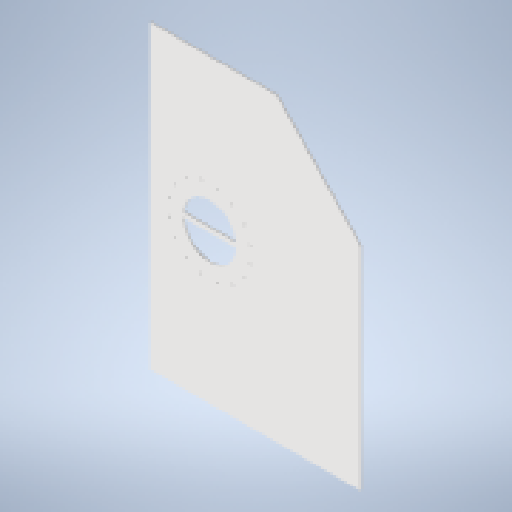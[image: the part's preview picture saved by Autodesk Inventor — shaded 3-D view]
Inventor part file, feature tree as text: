
AUTODESK INVENTOR PART (.ipt)
format: ipt  version: 2024.2 (Build 282272000, 272)  size: 310,784 bytes
history: native  units: mm
features: extrude x3, sketch x2, fillet x1, pattern_circular x1, projected_geometry x1, other x1
ambient origin geometry x8: Origin, YZ Plane, XZ Plane, XY Plane, X Axis, Y Axis, Z Axis, Center Point
bodies: Solid1 (feature_tree)
feature tree (9):
  extrude  "Extrusion1"  Depth=1180.0mm
  fillet  "Fillet1"  Radius=1180.0mm
  extrude  "Extrusion4"  Depth=10.0mm
  pattern_circular  "Circular Pattern3"  Count=191  [1 undecoded]
  extrude  "Extrusion5"  [1 undecoded]
  sketch  "Sketch4"  dims[d1=840.0mm d3=1150.0mm d12=1180.0mm]
  sketch  "Sketch5"  dims[d13=950.0mm d14=110.0mm d15=1910.0mm d17=-521.637743mm d18=377.0mm d19=-269.216713mm d24=10.0mm d25=0.0mm d34=380.0mm d35=80.0mm d37=2140.0mm d52=530.0mm d53=5.0mm d54=10.0mm d55=30.0mm d56=10.0mm d59=265.0mm d60=13.0mm d61=1.963495mm d62=10.0mm d63=0.0mm d64=160.0mm d65=360.0deg d67=5.0mm d68=5.0mm d69=780.0mm d71=1078.0mm d72=340.0mm d73=1340.0mm d74=10.0mm d75=0.0mm d70=0.872665mm]
  projected_geometry  "Projected Loop1"
  other  "Definition1"
note: 2 required parameter values undecoded (feature->parameter linkage not recoverable at this tier; creation-order binding heuristic only, values carry confidence <= 0.55)
